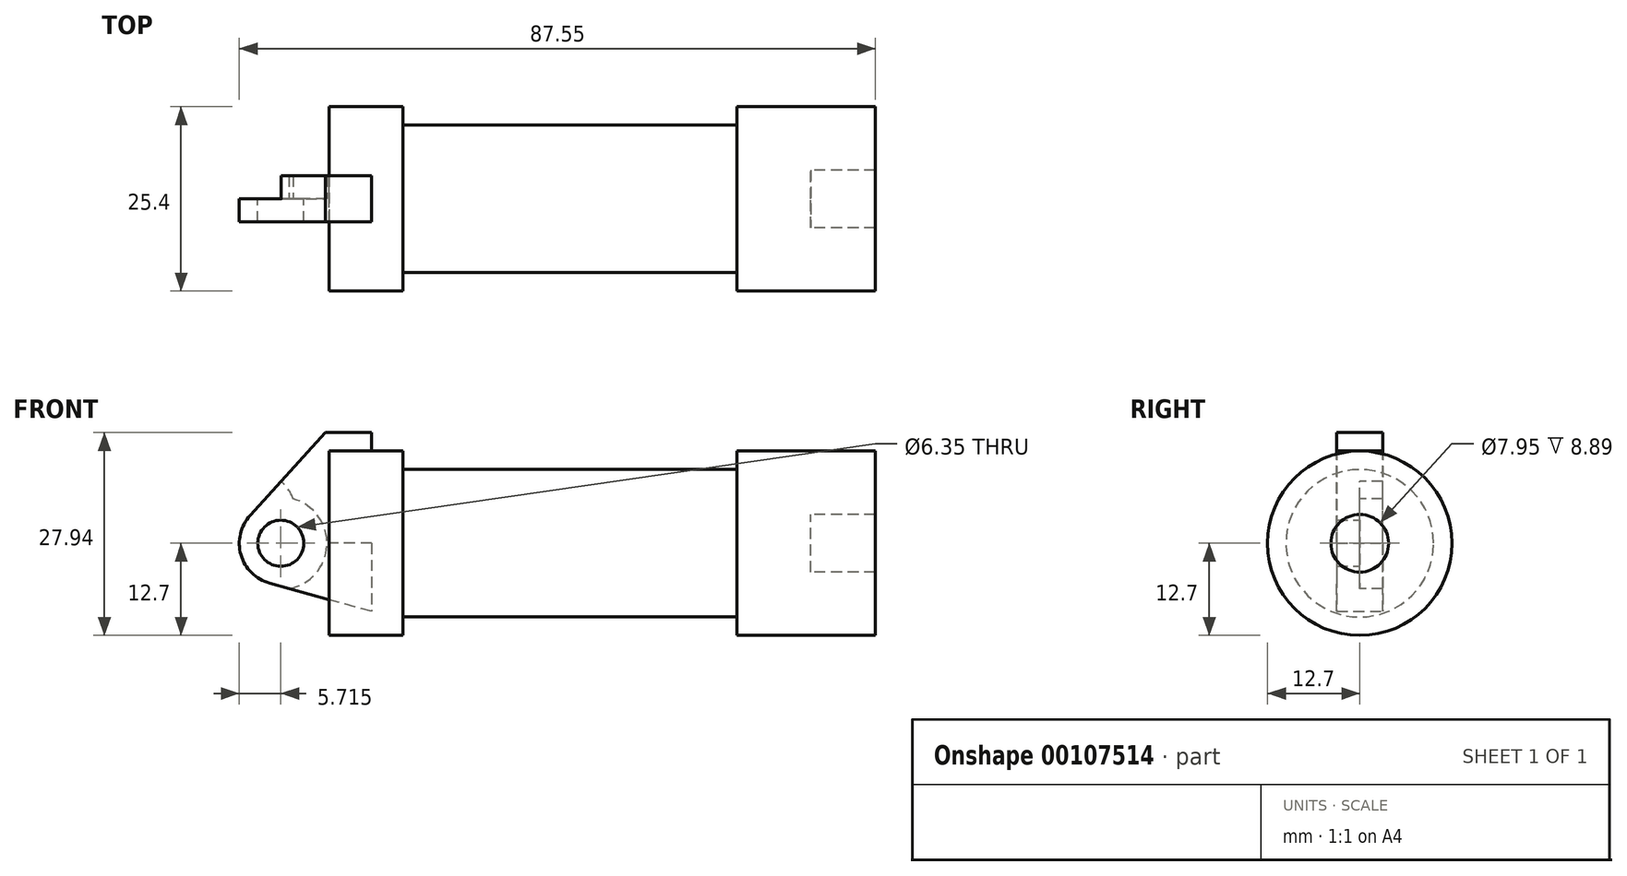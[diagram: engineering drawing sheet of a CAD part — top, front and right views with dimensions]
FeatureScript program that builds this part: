
annotation { "Feature Type Name" : "Feature", "Feature Type Description" : "" }
export const myFeature = defineFeature(function(context is Context, id is Id, definition is map)
    precondition{}
    {
        {
            var Q0;
            Q0=qCreatedBy(makeId("Front.planeOp"),FACE);
            var sketch = newSketch(context, id + "F0", { "sketchPlane" : qUnion([Q0])});
            skLineSegment(sketch, "E0", {"start": v(0, 0) * mm, "end": v(0, 12.7) * mm});
            skLineSegment(sketch, "E1", {"start": v(0, 12.7) * mm, "end": v(10.16, 12.7) * mm});
            skLineSegment(sketch, "E2", {"start": v(10.16, 12.7) * mm, "end": v(10.16, 10.16) * mm});
            skLineSegment(sketch, "E3", {"start": v(10.16, 10.16) * mm, "end": v(56.13, 10.16) * mm});
            skLineSegment(sketch, "E4", {"start": v(56.13, 10.16) * mm, "end": v(56.13, 12.7) * mm});
            skLineSegment(sketch, "E5", {"start": v(56.13, 12.7) * mm, "end": v(66.3, 12.7) * mm});
            skLineSegment(sketch, "E6", {"start": v(66.3, 12.7) * mm, "end": v(66.3, 0) * mm});
            skLineSegment(sketch, "E7", {"start": v(66.3, 0) * mm, "end": v(0, 0) * mm});
            skLineSegment(sketch, "E8", {"start": v(5.84, 15.24) * mm, "end": v(-0.5, 15.24) * mm});
            skLineSegment(sketch, "E9", {"start": v(-0.5, 15.24) * mm, "end": v(-10.88, 3.85) * mm});
            skLineSegment(sketch, "E10", {"start": v(0, 0) * mm, "end": v(-6.65, 0) * mm});
            skCircle(sketch, "E11", {"center": v(-6.65, 0) * mm, "radius": 5.72 * mm});
            skCircle(sketch, "E12", {"center": v(-6.65, 0) * mm, "radius": 3.18 * mm});
            skLineSegment(sketch, "E13", {"start": v(5.84, 15.24) * mm, "end": v(5.84, -9.4) * mm});
            skLineSegment(sketch, "E14", {"start": v(5.84, -9.4) * mm, "end": v(-8.18, -5.5) * mm});
            skSolve(sketch);
        }
        {
            var Q0;
            {var subQ0=sQuery(id+"F0.wireOp",EDGE,"E0");Q0=makeQuery(id+"F0.imprint","IMPRINT",FACE,{"disambiguationData":[TD([[makeQuery(id+"F0.imprint","IMPRINT",EDGE,{"derivedFrom":subQ0}),-1.0]])]});}
            var Q1;
            {var subQ0=sQuery(id+"F0.wireOp",EDGE,"E2");Q1=makeQuery(id+"F0.imprint","IMPRINT",FACE,{"disambiguationData":[TD([[makeQuery(id+"F0.imprint","IMPRINT",EDGE,{"derivedFrom":subQ0}),-1.0]])]});}
            var Q2;
            Q2=sQuery(id+"F0.wireOp",EDGE,"E7");
            revolve(context, id + "F1", {"entities" : qUnion([Q0, Q1]), "axis" : qUnion([Q2]), "revolveType" : RevolveType.FULL});
        }
        {
            var Q0;
            {var subQ3=sQuery(id+"F0.wireOp",EDGE,"E0");Q0=makeQuery(id+"F0.imprint","IMPRINT",FACE,{"disambiguationData":[TD([[makeQuery(id+"F0.imprint","IMPRINT",EDGE,{"derivedFrom":subQ3}),1.0]])]});}
            var Q1;
            {var subQ4=sQuery(id+"F0.wireOp",EDGE,"E12");Q1=makeQuery(id+"F0.imprint","IMPRINT",FACE,{"disambiguationData":[TD([[makeQuery(id+"F0.imprint","IMPRINT",EDGE,{"derivedFrom":subQ4}),-1.0]])]});}
            var Q2;
            {var subQ0=sQuery(id+"F0.wireOp",EDGE,"E14");Q2=makeQuery(id+"F0.imprint","IMPRINT",FACE,{"disambiguationData":[TD([[makeQuery(id+"F0.imprint","IMPRINT",EDGE,{"derivedFrom":subQ0}),-1.0]])]});}
            extrude(context, id + "F2", {"entities" : qUnion([Q0, Q1, Q2]), "endBound" : BoundingType.SYMMETRIC, "depth" : 6.35 * mm});
        }
        {
            var Q0;
            Q0=sQuery(id+"F0.wireOp",VERTEX,"E9.end");
            var Q1;
            Q1=sQuery(id+"F0.wireOp",VERTEX,"E12.center");
            var Q2;
            Q2=makeQuery(id+"F2.opExtrude","SWEPT_BODY",BODY,{"disambiguationData":[OSD([sQuery(id+"F0.wireOp",EDGE,"E0"),sQuery(id+"F0.wireOp",EDGE,"E1"),sQuery(id+"F0.wireOp",EDGE,"E7"),sQuery(id+"F0.wireOp",EDGE,"E8"),sQuery(id+"F0.wireOp",EDGE,"E9"),sQuery(id+"F0.wireOp",EDGE,"E11"),sQuery(id+"F0.wireOp",EDGE,"E12"),sQuery(id+"F0.wireOp",EDGE,"E13"),sQuery(id+"F0.wireOp",EDGE,"E14")])]});
            hole(context, id + "F3", {"style" : HoleStyle.C_BORE, "endStyle" : HoleEndStyle.BLIND, "holeDiameter" : 6.35 * mm, "cBoreDiameter" : 12.7 * mm, "cBoreDepth" : 6.35 * mm, "holeDepth" : 12.7 * mm, "locations" : qUnion([Q0, Q1]), "scope" : qUnion([Q2])});
        }
        {
            var Q0;
            Q0=makeQuery(id+"F1.opRevolve","SWEPT_FACE",FACE,{"disambiguationData":[OSD([sQuery(id+"F0.wireOp",EDGE,"E6")])]});
            var sketch = newSketch(context, id + "F4", { "sketchPlane" : qUnion([Q0])});
            skCircle(sketch, "E15", {"center": v(0, 0) * mm, "radius": 3.97 * mm});
            skCircle(sketch, "E16", {"center": v(0, 0) * mm, "radius": 1.33 * mm});
            skSolve(sketch);
        }
        {
            var Q0;
            Q0=makeQuery(id+"F4.imprint","IMPRINT",FACE,{"disambiguationData":[TD([[makeQuery(id+"F4.imprint","IMPRINT",EDGE,{"derivedFrom":sQuery(id+"F4.wireOp",EDGE,"E15")}),-1.0]])]});
            extrude(context, id + "F5", {"entities" : qUnion([Q0]), "operationType" : NewBodyOperationType.ADD, "depth" : 7.62 * mm});
        }
        {
            var Q0;
            Q0=makeQuery(id+"F5.opExtrude","CAP_FACE",FACE,{"disambiguationData":[OSD([sQuery(id+"F0.wireOp",EDGE,"E5"),sQuery(id+"F0.wireOp",EDGE,"E6"),sQuery(id+"F4.wireOp",EDGE,"E15")])],"isStart":false});
            extrude(context, id + "F6", {"entities" : qUnion([Q0]), "operationType" : NewBodyOperationType.ADD, "depth" : 1.27 * mm});
        }
    });
